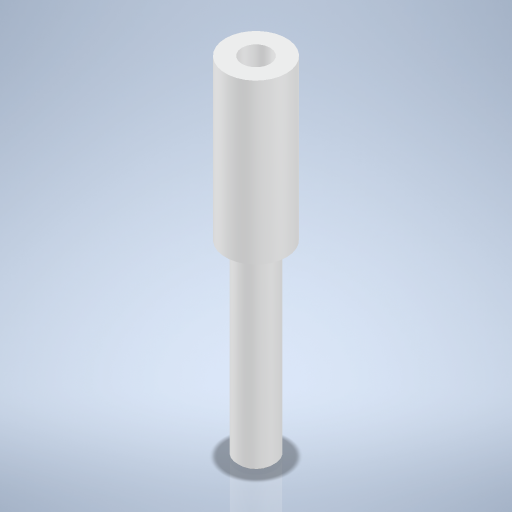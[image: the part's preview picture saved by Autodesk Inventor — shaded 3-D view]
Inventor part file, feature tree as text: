
AUTODESK INVENTOR PART (.ipt)
format: ipt  version: 2024 (Build 280153000, 153)  size: 251,904 bytes
history: native  units: mm
features: sketch x2, revolve x1, chamfer x1, hole x1
ambient origin geometry x8: Origin, YZ Plane, XZ Plane, XY Plane, X Axis, Y Axis, Z Axis, Center Point
bodies: Body1 (feature_tree)
feature tree (5):
  revolve  "Umdrehung1"
  chamfer  "Fasen1"  Distance=34.0mm
  hole  "Bohrung1"  [1 undecoded]
  sketch  "Skizze2"  dims[d3=13.0mm]
  sketch  "Skizze3"  dims[d4=8.0mm d5=34.0mm d6=40.0mm d7=90.0deg d8=0.6mm d9=2.0mm d10=45.0deg d11=6.0mm d12=8.0mm d13=4.0mm d14=2.0mm d15=90.0deg d16=34.0mm d17=0.0mm]
note: 1 required parameter value undecoded (feature->parameter linkage not recoverable at this tier; creation-order binding heuristic only, values carry confidence <= 0.55)
